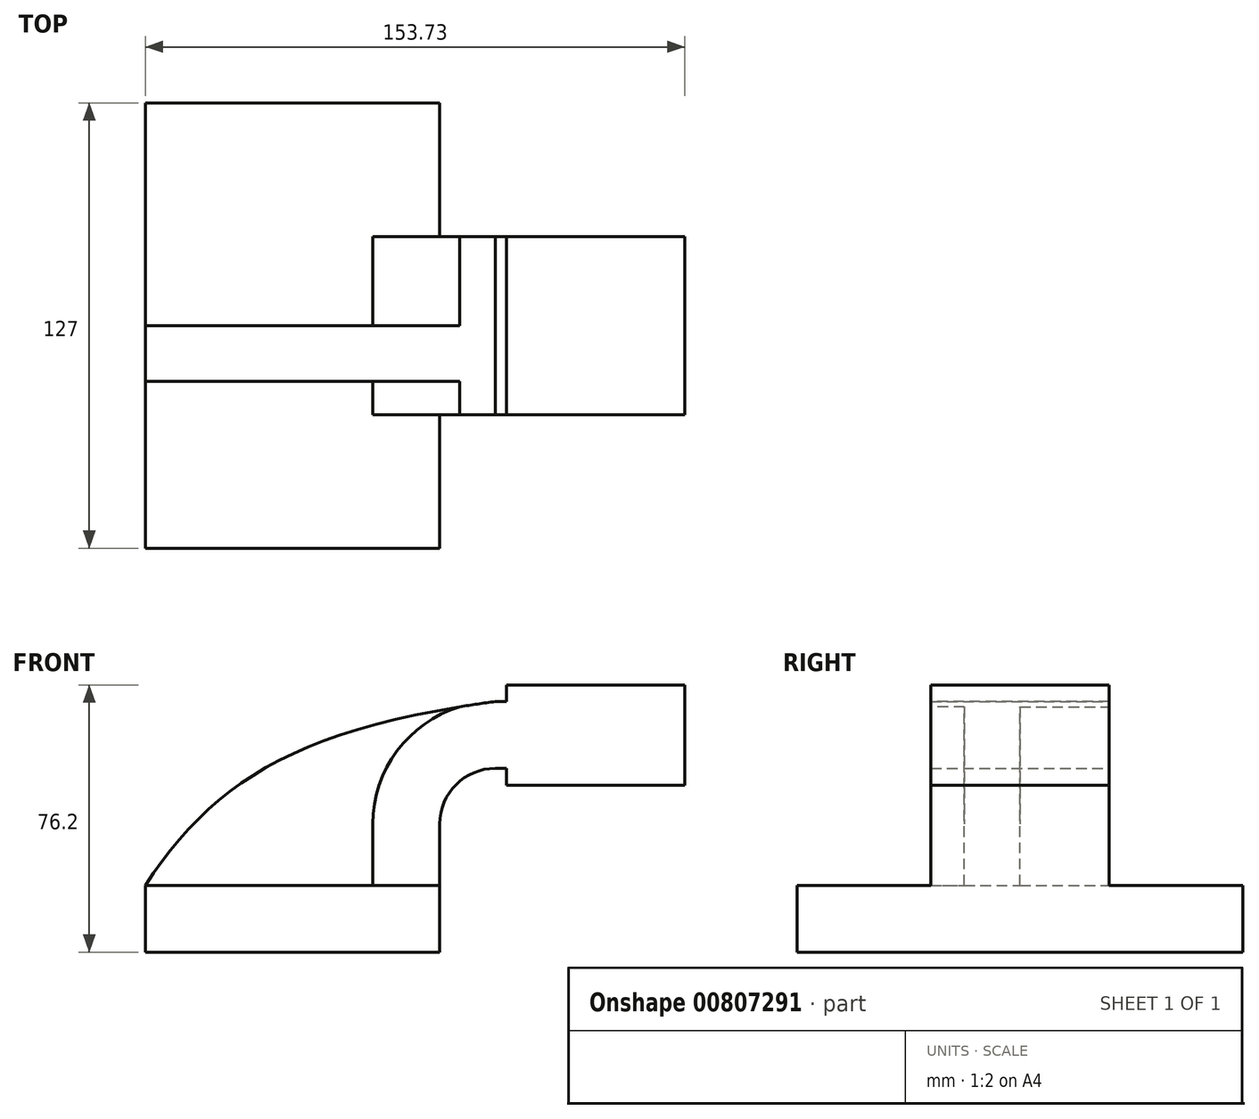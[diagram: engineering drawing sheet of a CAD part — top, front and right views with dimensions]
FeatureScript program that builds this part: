
annotation { "Feature Type Name" : "Feature", "Feature Type Description" : "" }
export const myFeature = defineFeature(function(context is Context, id is Id, definition is map)
    precondition{}
    {
        {
            var Q0;
            Q0=qCreatedBy(makeId("Front.planeOp"),FACE);
            var sketch = newSketch(context, id + "F0", { "sketchPlane" : qUnion([Q0])});
            skLineSegment(sketch, "E0.bottom", {"start": v(41.94, -9.52) * mm, "end": v(-41.94, -9.53) * mm});
            skLineSegment(sketch, "E0.top", {"start": v(41.94, 9.53) * mm, "end": v(-41.94, 9.53) * mm});
            skLineSegment(sketch, "E0.left", {"start": v(41.94, -9.52) * mm, "end": v(41.94, 9.53) * mm});
            skLineSegment(sketch, "E0.right", {"start": v(-41.94, -9.53) * mm, "end": v(-41.94, 9.53) * mm});
            skPoint(sketch, "E0.middle", {"position": v(0, 0) * mm});
            skLineSegment(sketch, "E1.bottom", {"start": v(111.8, 38.1) * mm, "end": v(61, 38.1) * mm});
            skLineSegment(sketch, "E1.top", {"start": v(111.8, 66.68) * mm, "end": v(61, 66.68) * mm});
            skLineSegment(sketch, "E1.left", {"start": v(111.8, 38.1) * mm, "end": v(111.8, 66.68) * mm});
            skLineSegment(sketch, "E1.right", {"start": v(61, 38.1) * mm, "end": v(61, 66.68) * mm});
            skPoint(sketch, "E1.middle", {"position": v(86.4, 52.39) * mm});
            skLineSegment(sketch, "E2", {"start": v(41.94, 9.53) * mm, "end": v(41.94, 27) * mm});
            skArc(sketch, "E3", {"start": v(41.94, 27) * mm, "mid": v(46.6, 38.23) * mm, "end": v(57.82, 42.88) * mm});
            skLineSegment(sketch, "E4", {"start": v(57.82, 42.88) * mm, "end": v(86.4, 42.88) * mm});
            skArc(sketch, "E5.0", {"start": v(22.9, 27) * mm, "mid": v(33.12, 51.7) * mm, "end": v(57.82, 61.93) * mm});
            skLineSegment(sketch, "E5.1", {"start": v(22.9, 9.53) * mm, "end": v(22.9, 27) * mm});
            skLineSegment(sketch, "E6", {"start": v(86.4, 38.1) * mm, "end": v(86.4, 66.68) * mm});
            skLineSegment(sketch, "E7", {"start": v(57.82, 61.93) * mm, "end": v(86.4, 61.93) * mm});
            skFitSpline(sketch, "E8", {"points": [v(-41.94, 9.53) * mm, v(57.82, 61.93) * mm], "startDerivative": vector(56.65, 86.36) * mm, "endDerivative": vector(173.45, 23.46) * mm});
            skSolve(sketch);
        }
        {
            var Q0;
            Q0=makeQuery(id+"F0.imprint","IMPRINT",FACE,{"disambiguationData":[TD([[makeQuery(id+"F0.imprint","IMPRINT",EDGE,{"derivedFrom":sQuery(id+"F0.wireOp",EDGE,"E0.bottom")}),-1.0]])]});
            extrude(context, id + "F1", {"entities" : qUnion([Q0]), "endBound" : BoundingType.SYMMETRIC, "depth" : 127 * mm, "offsetDistance" : 25.4 * mm});
        }
        {
            var Q0;
            {var subQ1=sQuery(id+"F0.wireOp",EDGE,"E2");Q0=makeQuery(id+"F0.imprint","IMPRINT",FACE,{"disambiguationData":[TD([[makeQuery(id+"F0.imprint","IMPRINT",EDGE,{"derivedFrom":subQ1}),1.0]])]});}
            var Q1;
            {var subQ0=sQuery(id+"F0.wireOp",EDGE,"E1.right");var subQ1=sQuery(id+"F0.wireOp",EDGE,"E1.bottom");var subQ2=makeQuery(id+"F0.imprint","INTERSECT",VERTEX,{"derivedFrom":[subQ1,subQ0]});Q1=makeQuery(id+"F0.imprint","IMPRINT",FACE,{"disambiguationData":[TD([[makeQuery(id+"F0.imprint","IMPRINT",EDGE,{"disambiguationData":[TD([[subQ2,1.0]])],"derivedFrom":subQ1}),-1.0]])]});}
            var Q2;
            {var subQ0=sQuery(id+"F0.wireOp",EDGE,"E1.right");var subQ1=sQuery(id+"F0.wireOp",EDGE,"E1.top");var subQ2=makeQuery(id+"F0.imprint","INTERSECT",VERTEX,{"derivedFrom":[subQ1,subQ0]});Q2=makeQuery(id+"F0.imprint","IMPRINT",FACE,{"disambiguationData":[TD([[makeQuery(id+"F0.imprint","IMPRINT",EDGE,{"disambiguationData":[TD([[subQ2,1.0]])],"derivedFrom":subQ1}),1.0]])]});}
            var Q3;
            {var subQ0=sQuery(id+"F0.wireOp",EDGE,"E4");var subQ1=sQuery(id+"F0.wireOp",EDGE,"E1.right");var subQ2=makeQuery(id+"F0.imprint","INTERSECT",VERTEX,{"derivedFrom":[subQ1,subQ0]});Q3=makeQuery(id+"F0.imprint","IMPRINT",FACE,{"disambiguationData":[TD([[makeQuery(id+"F0.imprint","IMPRINT",EDGE,{"disambiguationData":[TD([[subQ2,-1.0]])],"derivedFrom":subQ1}),-1.0]])]});}
            var Q4;
            {var subQ0=sQuery(id+"F0.wireOp",EDGE,"E1.left");Q4=makeQuery(id+"F0.imprint","IMPRINT",FACE,{"disambiguationData":[TD([[makeQuery(id+"F0.imprint","IMPRINT",EDGE,{"derivedFrom":subQ0}),1.0]])]});}
            extrude(context, id + "F2", {"entities" : qUnion([Q0, Q1, Q2, Q3, Q4]), "operationType" : NewBodyOperationType.ADD, "endBound" : BoundingType.SYMMETRIC, "depth" : 50.8 * mm, "offsetDistance" : 25.4 * mm});
        }
        {
            var Q0;
            {var subQ3=sQuery(id+"F0.wireOp",EDGE,"E5.1");Q0=makeQuery(id+"F0.imprint","IMPRINT",FACE,{"disambiguationData":[TD([[makeQuery(id+"F0.imprint","IMPRINT",EDGE,{"derivedFrom":subQ3}),1.0]])]});}
            extrude(context, id + "F3", {"entities" : qUnion([Q0]), "operationType" : NewBodyOperationType.ADD, "depth" : 15.88 * mm, "offsetDistance" : 25.4 * mm});
        }
    });
